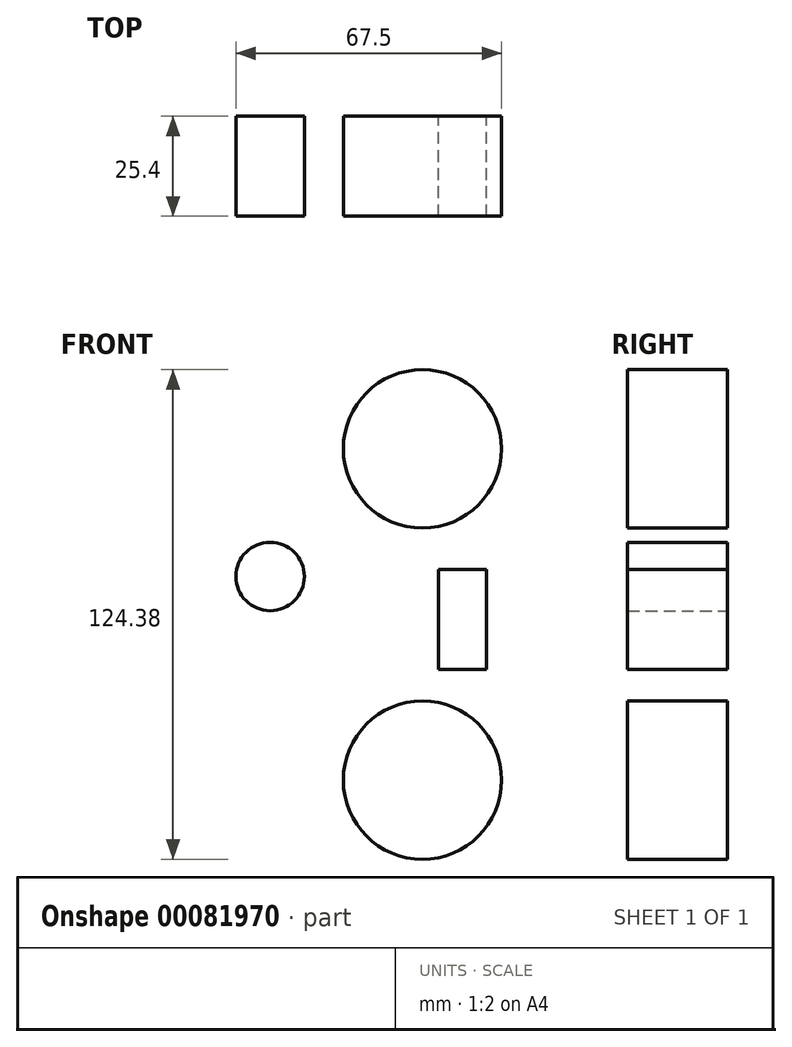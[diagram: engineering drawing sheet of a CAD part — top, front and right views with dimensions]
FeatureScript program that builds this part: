
annotation { "Feature Type Name" : "Feature", "Feature Type Description" : "" }
export const myFeature = defineFeature(function(context is Context, id is Id, definition is map)
    precondition{}
    {
        {
            var Q0;
            Q0=qCreatedBy(makeId("Front.planeOp"),FACE);
            var sketch = newSketch(context, id + "F0", { "sketchPlane" : qUnion([Q0])});
            skCircle(sketch, "E0", {"center": v(0, 56.04) * mm, "radius": 20.1 * mm});
            skCircle(sketch, "E1", {"center": v(0, -28.14) * mm, "radius": 20.1 * mm});
            skCircle(sketch, "E2", {"center": v(-38.7, 23.6) * mm, "radius": 8.7 * mm});
            skLineSegment(sketch, "E3", {"start": v(-16.07, 68.13) * mm, "end": v(-45.64, 28.83) * mm});
            skLineSegment(sketch, "E4", {"start": v(20.1, -28.14) * mm, "end": v(20.1, 56.04) * mm});
            skLineSegment(sketch, "E5", {"start": v(-46.47, 19.7) * mm, "end": v(-17.98, -37.15) * mm});
            skLineSegment(sketch, "E6.bottom", {"start": v(4.08, 25.4) * mm, "end": v(16.3, 25.4) * mm});
            skLineSegment(sketch, "E6.top", {"start": v(4.08, 0) * mm, "end": v(16.3, 0) * mm});
            skLineSegment(sketch, "E6.left", {"start": v(4.08, 25.4) * mm, "end": v(4.08, 0) * mm});
            skLineSegment(sketch, "E6.right", {"start": v(16.3, 25.4) * mm, "end": v(16.3, 0) * mm});
            skSolve(sketch);
        }
        {
            var Q0;
            {var subQ0=sQuery(id+"F0.wireOp",EDGE,"E0");var subQ1=makeQuery(id+"F0.imprint","INTERSECT",VERTEX,{"derivedFrom":[subQ0,sQuery(id+"F0.wireOp",EDGE,"E3")]});Q0=makeQuery(id+"F0.imprint","IMPRINT",FACE,{"disambiguationData":[TD([[makeQuery(id+"F0.imprint","IMPRINT",EDGE,{"disambiguationData":[TD([[subQ1,1.0]])],"derivedFrom":subQ0}),1.0]])]});}
            var Q1;
            {var subQ0=sQuery(id+"F0.wireOp",EDGE,"E1");var subQ1=makeQuery(id+"F0.imprint","INTERSECT",VERTEX,{"derivedFrom":[subQ0,sQuery(id+"F0.wireOp",EDGE,"E4")]});Q1=makeQuery(id+"F0.imprint","IMPRINT",FACE,{"disambiguationData":[TD([[makeQuery(id+"F0.imprint","IMPRINT",EDGE,{"disambiguationData":[TD([[subQ1,-1.0]])],"derivedFrom":subQ0}),1.0]])]});}
            var Q2;
            {var subQ0=sQuery(id+"F0.wireOp",EDGE,"E2");var subQ1=makeQuery(id+"F0.imprint","INTERSECT",VERTEX,{"derivedFrom":[subQ0,sQuery(id+"F0.wireOp",EDGE,"E3")]});Q2=makeQuery(id+"F0.imprint","IMPRINT",FACE,{"disambiguationData":[TD([[makeQuery(id+"F0.imprint","IMPRINT",EDGE,{"disambiguationData":[TD([[subQ1,-1.0]])],"derivedFrom":subQ0}),1.0]])]});}
            var Q3;
            Q3=makeQuery(id+"F0.imprint","IMPRINT",FACE,{"disambiguationData":[TD([[makeQuery(id+"F0.imprint","IMPRINT",EDGE,{"derivedFrom":sQuery(id+"F0.wireOp",EDGE,"E6.bottom")}),-1.0]])]});
            extrude(context, id + "F1", {"entities" : qUnion([Q0, Q1, Q2, Q3]), "depth" : 25.4 * mm});
        }
    });
